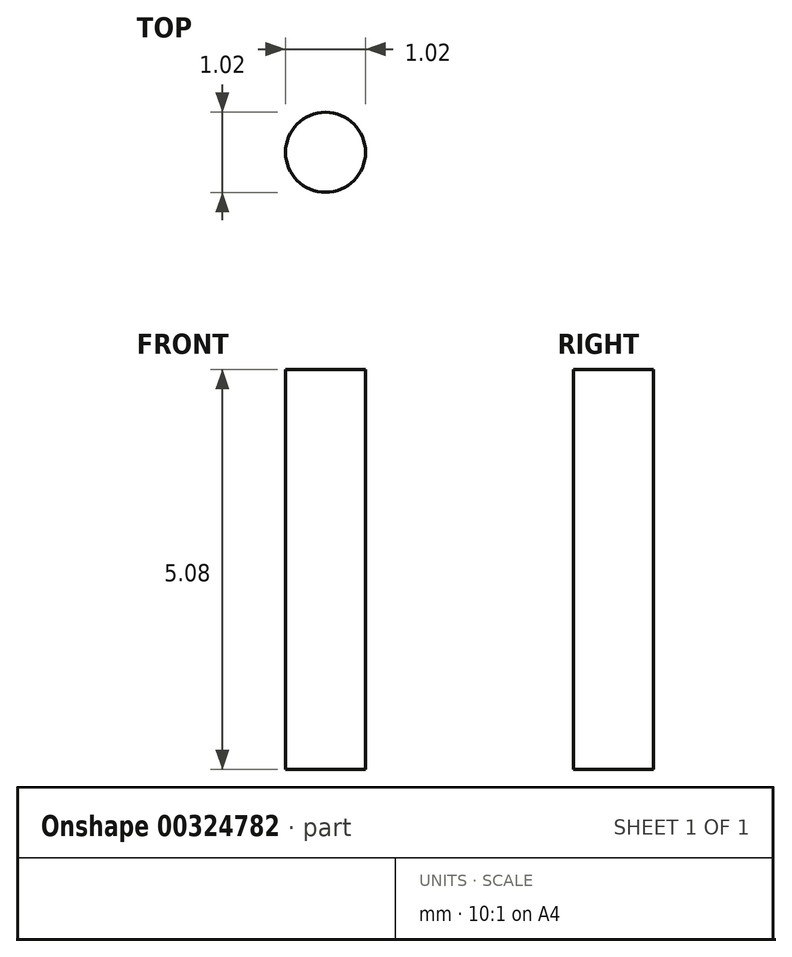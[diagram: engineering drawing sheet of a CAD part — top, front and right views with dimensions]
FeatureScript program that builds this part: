
annotation { "Feature Type Name" : "Feature", "Feature Type Description" : "" }
export const myFeature = defineFeature(function(context is Context, id is Id, definition is map)
    precondition{}
    {
        {
            var Q0;
            Q0=qCreatedBy(makeId("Top.planeOp"),FACE);
            var sketch = newSketch(context, id + "F0", { "sketchPlane" : qUnion([Q0])});
            skCircle(sketch, "E0", {"center": v(0, 0) * mm, "radius": 0.5 * mm});
            skSolve(sketch);
        }
        {
            var Q0;
            Q0=makeQuery(id+"F0.imprint","IMPRINT",FACE,{"disambiguationData":[TD([[makeQuery(id+"F0.imprint","IMPRINT",EDGE,{"derivedFrom":sQuery(id+"F0.wireOp",EDGE,"E0")}),1.0]])]});
            extrude(context, id + "F1", {"entities" : qUnion([Q0]), "depth" : 5.08 * mm, "offsetDistance" : 25.4 * mm});
        }
    });
